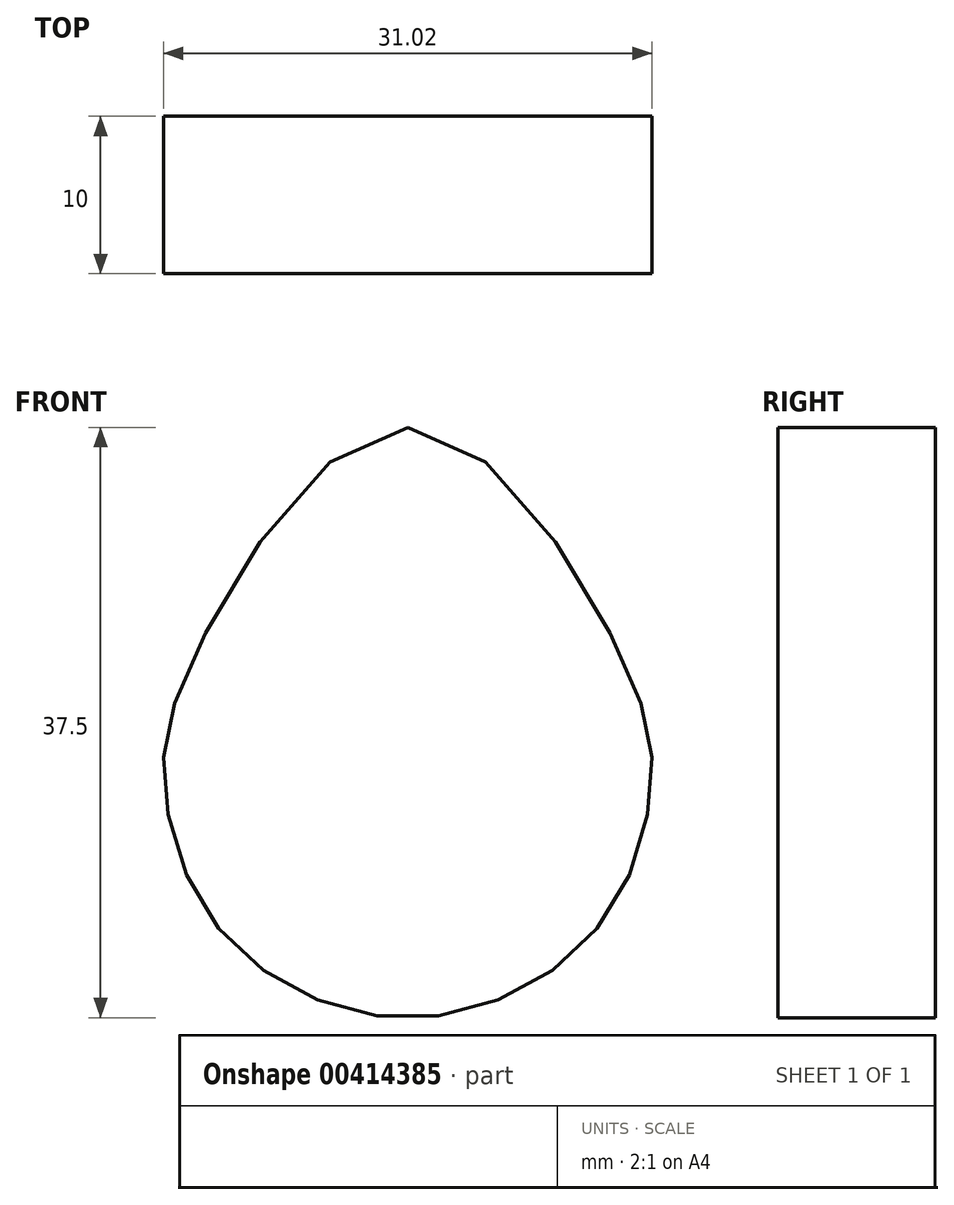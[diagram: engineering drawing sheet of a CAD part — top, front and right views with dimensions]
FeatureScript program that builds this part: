
annotation { "Feature Type Name" : "Feature", "Feature Type Description" : "" }
export const myFeature = defineFeature(function(context is Context, id is Id, definition is map)
    precondition{}
    {
        {
            var Q0;
            Q0=qCreatedBy(makeId("Front.planeOp"),FACE);
            var sketch = newSketch(context, id + "F0", { "sketchPlane" : qUnion([Q0])});
            skCircle(sketch, "E0", {"center": v(0, 0) * mm, "radius": 15.5 * mm, "construction": true});
            skCircle(sketch, "E1", {"center": v(0, 0) * mm, "radius": 22 * mm, "construction": true});
            skLineSegment(sketch, "E2", {"start": v(0, 0) * mm, "end": v(42.98, 0) * mm, "construction": true});
            skLineSegment(sketch, "E3", {"start": v(0, 0) * mm, "end": v(0, 34.96) * mm, "construction": true});
            skLineSegment(sketch, "E4", {"start": v(0, 0) * mm, "end": v(-36, 0) * mm, "construction": true});
            skLineSegment(sketch, "E5", {"start": v(0, 0) * mm, "end": v(0, -28.74) * mm, "construction": true});
            skPoint(sketch, "E6", {"position": v(0, 22) * mm});
            skLineSegment(sketch, "E7", {"start": v(0, 0) * mm, "end": v(-30.08, -17.37) * mm, "construction": true});
            skLineSegment(sketch, "E8", {"start": v(0, 0) * mm, "end": v(-16.02, -27.75) * mm, "construction": true});
            skLineSegment(sketch, "E9", {"start": v(0, 0) * mm, "end": v(30.88, -17.83) * mm, "construction": true});
            skLineSegment(sketch, "E10", {"start": v(0, 0) * mm, "end": v(15.35, -26.59) * mm, "construction": true});
            skPoint(sketch, "E11", {"position": v(-13.42, -7.75) * mm});
            skPoint(sketch, "E12", {"position": v(-7.75, -13.42) * mm});
            skPoint(sketch, "E13", {"position": v(13.42, -7.75) * mm});
            skPoint(sketch, "E14", {"position": v(7.75, -13.42) * mm});
            skPoint(sketch, "E15", {"position": v(-15.5, 0) * mm});
            skPoint(sketch, "E16", {"position": v(15.5, 0) * mm});
            skLineSegment(sketch, "E17", {"start": v(0, 0) * mm, "end": v(-21.57, 12.45) * mm, "construction": true});
            skLineSegment(sketch, "E18", {"start": v(0, 0) * mm, "end": v(22.45, 12.96) * mm, "construction": true});
            skPoint(sketch, "E19", {"position": v(0, -15.5) * mm});
            skPoint(sketch, "E20", {"position": v(-13.42, 7.75) * mm});
            skPoint(sketch, "E21", {"position": v(13.42, 7.75) * mm});
            skFitSpline(sketch, "E22", {"points": [v(0, 22) * mm, v(-13.42, 7.75) * mm, v(-15.5, 0) * mm, v(-13.42, -7.75) * mm, v(-7.75, -13.42) * mm, v(0, -15.5) * mm, v(7.75, -13.42) * mm, v(13.42, -7.75) * mm, v(15.5, 0) * mm, v(13.42, 7.75) * mm, v(0, 22) * mm]});
            skSolve(sketch);
        }
        {
            var Q0;
            Q0 = qSketchRegion(id + "F0", true);
            extrude(context, id + "F1", {"entities" : qUnion([Q0]), "depth" : 10 * mm});
        }
    });
